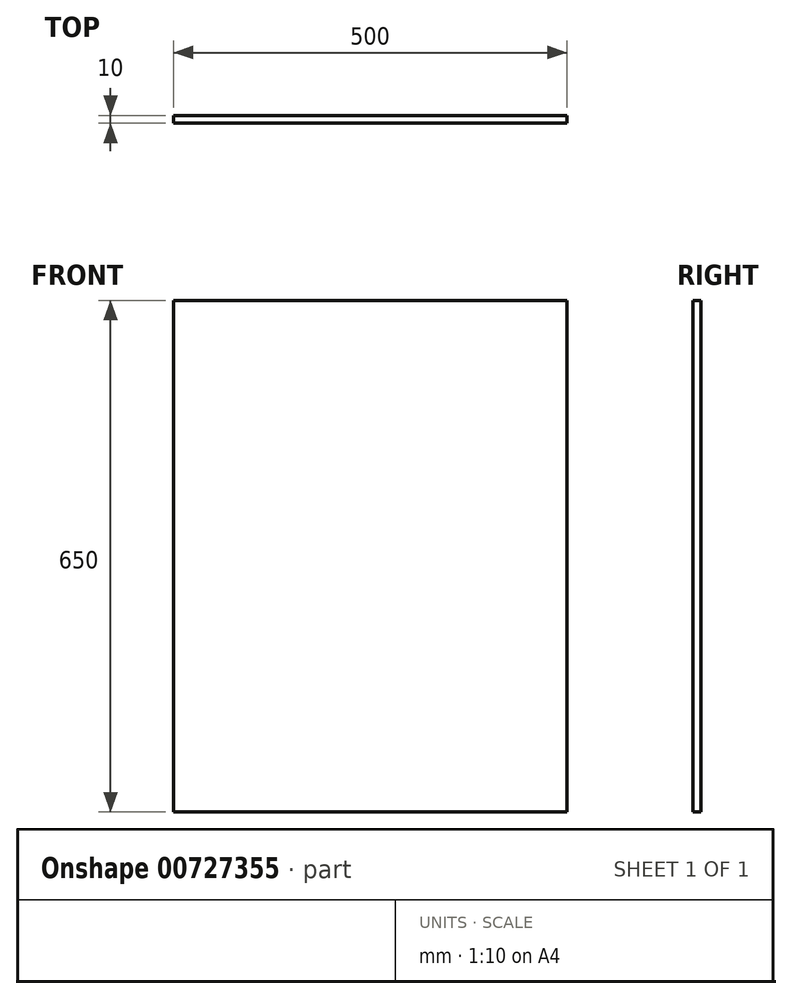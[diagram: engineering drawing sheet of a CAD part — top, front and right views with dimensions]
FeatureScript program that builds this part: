
annotation { "Feature Type Name" : "Feature", "Feature Type Description" : "" }
export const myFeature = defineFeature(function(context is Context, id is Id, definition is map)
    precondition{}
    {
        {
            var Q0;
            Q0=qCreatedBy(makeId("Front.planeOp"),FACE);
            var sketch = newSketch(context, id + "F0", { "sketchPlane" : qUnion([Q0])});
            skLineSegment(sketch, "E0.bottom", {"start": v(0, 0) * mm, "end": v(500, 0) * mm});
            skLineSegment(sketch, "E0.top", {"start": v(0, 650) * mm, "end": v(500, 650) * mm});
            skLineSegment(sketch, "E0.left", {"start": v(0, 0) * mm, "end": v(0, 650) * mm});
            skLineSegment(sketch, "E0.right", {"start": v(500, 0) * mm, "end": v(500, 650) * mm});
            skSolve(sketch);
        }
        {
            var Q0;
            Q0 = qSketchRegion(id + "F0", true);
            extrude(context, id + "F1", {"entities" : qUnion([Q0]), "depth" : 10 * mm, "offsetDistance" : 25 * mm});
        }
    });
